# Revit family: Urinal-Wall-Caroma Integra Invisi II
name_source: partatom
category: Plumbing Fixtures
revit_build: Autodesk Revit 2014 (Build: 20131024_2115(x64)
units: mm (PartAtom-declared; Revit-internal decimal feet)

## types (1)
- Standard
    Assembly Code = C1030210
    CW Connection = Yes
    CWFU = 1
    Cost = 0 $
    Default Elevation = 610 mm
    Description = Caroma Integra Urinal Invisi Series II Suite
    HW Connection = No
    Hardware = Metal-Chrome-Caroma
    Height_ANZRS = 648 mm
    Keynote = UR
    Length_ANZRS = 375 mm
    Manufacturer = GWA Bathrooms & Kitchens
    Material_ANZRS = Porcelain-White-Caroma
    Model = 743100W
    ModifiedIssue_ANZRS = 20140917.01 $
    Type Comments = Available for Induct, Inceiling & Inwall installations, Buttons and panels Sold Separately
    URL = http://www.caroma.com.au
    Vent Connection = No
    WELSRating_ANZRS = WELS 3 Star rated, 6/3L
    WFU = 1
    Waste Connection = Yes
    Width_ANZRS = 385 mm

## geometry (parser evidence)
native form markers: Blend x6, Sweep x2
no freeform markers — native parametric forms only
